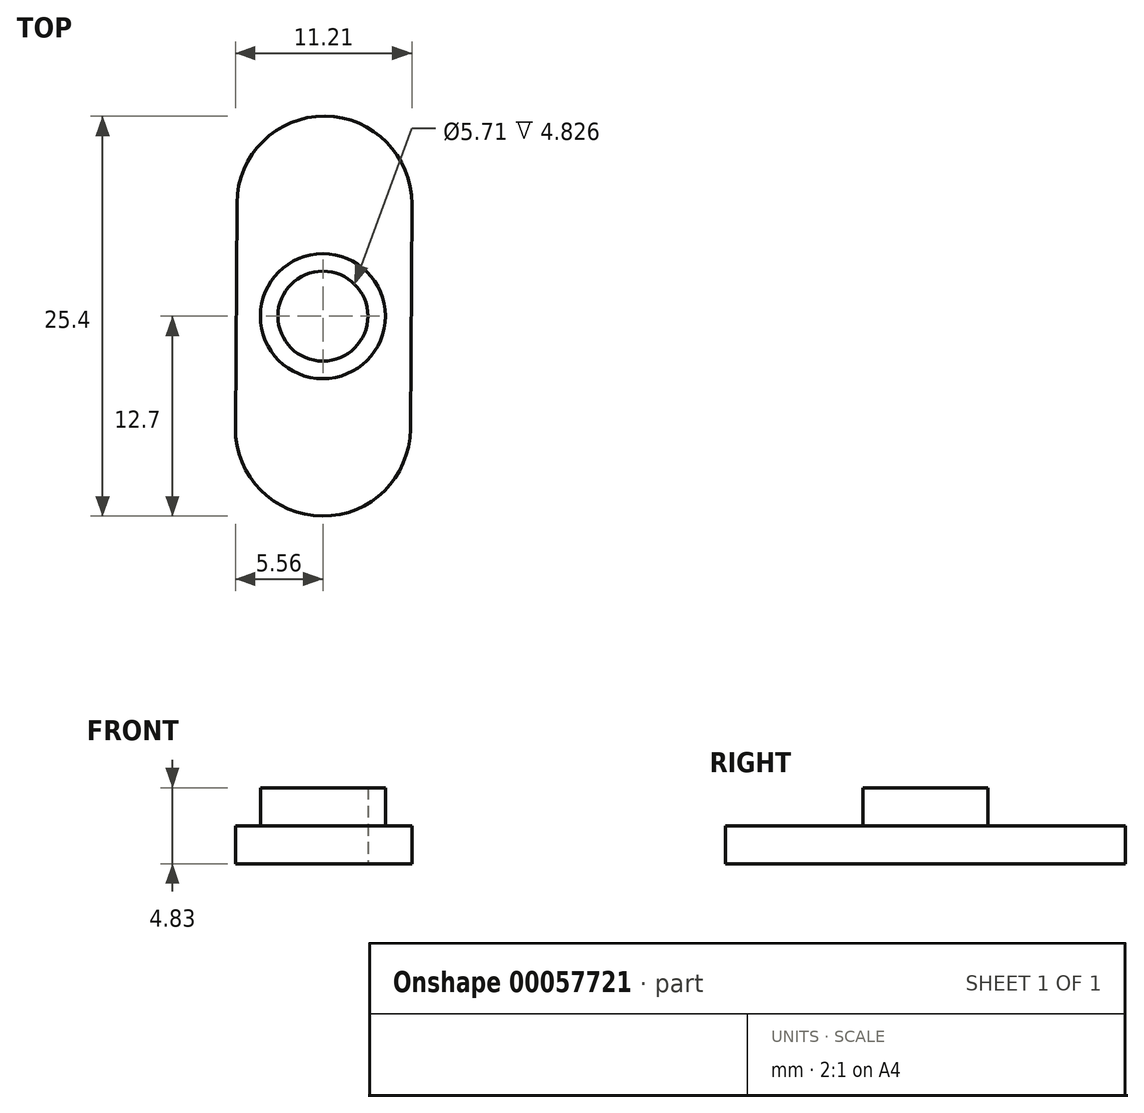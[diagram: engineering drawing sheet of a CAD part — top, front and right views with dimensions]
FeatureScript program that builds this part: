
annotation { "Feature Type Name" : "Feature", "Feature Type Description" : "" }
export const myFeature = defineFeature(function(context is Context, id is Id, definition is map)
    precondition{}
    {
        {
            var Q0;
            Q0=qCreatedBy(makeId("Top.planeOp"),FACE);
            var sketch = newSketch(context, id + "F0", { "sketchPlane" : qUnion([Q0])});
            skLineSegment(sketch, "E0.left", {"start": v(-5.46, 7.18) * mm, "end": v(-5.56, -7.1) * mm});
            skLineSegment(sketch, "E0.right", {"start": v(5.65, 7.1) * mm, "end": v(5.56, -7.18) * mm});
            skArc(sketch, "E1", {"start": v(5.65, 7.1) * mm, "mid": v(0.13, 12.7) * mm, "end": v(-5.46, 7.18) * mm});
            skArc(sketch, "E2", {"start": v(-5.56, -7.1) * mm, "mid": v(-0.02, -12.7) * mm, "end": v(5.56, -7.14) * mm});
            skCircle(sketch, "E3", {"center": v(0, 0) * mm, "radius": 3.97 * mm});
            skCircle(sketch, "E4", {"center": v(0, 0) * mm, "radius": 2.86 * mm});
            skSolve(sketch);
        }
        {
            var Q0;
            Q0=makeQuery(id+"F0.imprint","IMPRINT",FACE,{"disambiguationData":[TD([[makeQuery(id+"F0.imprint","IMPRINT",EDGE,{"derivedFrom":sQuery(id+"F0.wireOp",EDGE,"E3")}),1.0]])]});
            extrude(context, id + "F1", {"entities" : qUnion([Q0]), "depth" : 4.83 * mm});
        }
        {
            var Q0;
            Q0=makeQuery(id+"F0.imprint","IMPRINT",FACE,{"disambiguationData":[TD([[makeQuery(id+"F0.imprint","IMPRINT",EDGE,{"derivedFrom":sQuery(id+"F0.wireOp",EDGE,"E0.left")}),1.0]])]});
            extrude(context, id + "F2", {"entities" : qUnion([Q0]), "operationType" : NewBodyOperationType.ADD, "depth" : 2.41 * mm});
        }
    });
